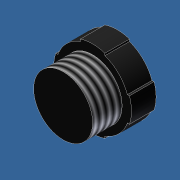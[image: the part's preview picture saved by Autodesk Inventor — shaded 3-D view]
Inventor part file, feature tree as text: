
AUTODESK INVENTOR PART (.ipt)
format: ipt  version: unknown  size: 204,288 bytes
history: native  units: in
note: dims shown in document units (in); Inventor stores cm internally (conversion verified against a paired STEP export)
features: extrude x3, sketch x3, thread x1
ambient origin geometry x8: Origin, YZ Plane, XZ Plane, XY Plane, X Axis, Y Axis, Z Axis, Center Point
bodies: Solid1 (feature_tree)
feature tree (7):
  extrude  "Extrusion1"  Depth=0.5in TaperAngle=0.0deg
  extrude  "Extrusion2"  Depth=0.25in
  extrude  "Extrusion3"  Depth=0.25in
  thread  "Thread1"  [1 undecoded]
  sketch  "Sketch1"  dims[d0=1.5in d1=0.5in d2=0.0in]
  sketch  "Sketch2"  dims[d3=0.5in d4=0.25in]
  sketch  "Sketch3"  dims[d5=0.5in d6=0.25in d7=0.5in d8=0.0in d9=1.2in d10=0.6in d11=0.0in d12=1.0in d13=0.0in]
note: 1 required parameter value undecoded (feature->parameter linkage not recoverable at this tier; creation-order binding heuristic only, values carry confidence <= 0.55)
